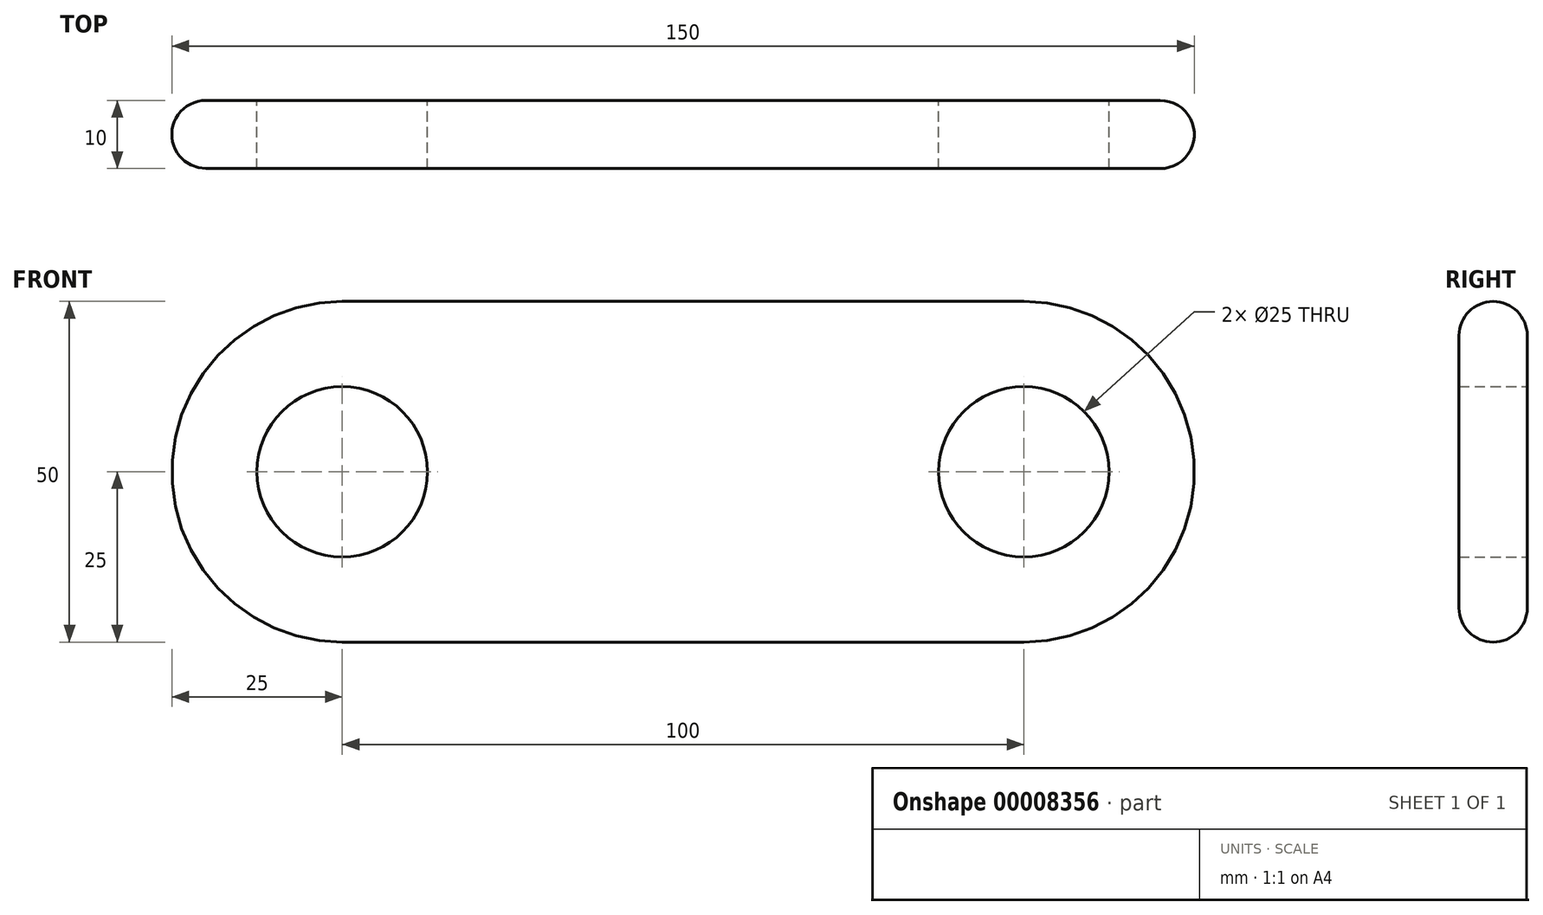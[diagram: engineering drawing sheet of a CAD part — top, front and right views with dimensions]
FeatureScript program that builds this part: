
annotation { "Feature Type Name" : "Feature", "Feature Type Description" : "" }
export const myFeature = defineFeature(function(context is Context, id is Id, definition is map)
    precondition{}
    {
        {
            var Q0;
            Q0=qCreatedBy(makeId("Front.planeOp"),FACE);
            var sketch = newSketch(context, id + "F0", { "sketchPlane" : qUnion([Q0])});
            skLineSegment(sketch, "E0.rect.bottom", {"start": v(50, 25) * mm, "end": v(-50, 25) * mm});
            skLineSegment(sketch, "E0.rect.top", {"start": v(50, -25) * mm, "end": v(-50, -25) * mm});
            skPoint(sketch, "E0.rect.middle", {"position": v(0, 0) * mm});
            skArc(sketch, "E1", {"start": v(-50, 25) * mm, "mid": v(-75, 0) * mm, "end": v(-50, -25) * mm});
            skArc(sketch, "E2", {"start": v(50, -25) * mm, "mid": v(75, 0) * mm, "end": v(50, 25) * mm});
            skCircle(sketch, "E3", {"center": v(-50, 0) * mm, "radius": 12.5 * mm});
            skCircle(sketch, "E4", {"center": v(50, 0) * mm, "radius": 12.5 * mm});
            skSolve(sketch);
        }
        {
            var Q0;
            Q0=makeQuery(id+"F0.imprint","IMPRINT",FACE,{"disambiguationData":[TD([[makeQuery(id+"F0.imprint","IMPRINT",EDGE,{"derivedFrom":sQuery(id+"F0.wireOp",EDGE,"E0.rect.bottom")}),1.0]])]});
            extrude(context, id + "F1", {"entities" : qUnion([Q0]), "depth" : 10 * mm});
        }
        {
            var Q0;
            Q0=makeQuery(id+"F1.opExtrude","CAP_EDGE",EDGE,{"disambiguationData":[OSD([sQuery(id+"F0.wireOp",EDGE,"E0.rect.top")])],"isStart":true});
            fillet(context, id + "F2", {"entities" : qUnion([Q0]), "radius" : 5 * mm, "tangentPropagation" : true, "allowEdgeOverflow" : false});
        }
        {
            var Q0;
            Q0=makeQuery(id+"F1.opExtrude","CAP_EDGE",EDGE,{"disambiguationData":[OSD([sQuery(id+"F0.wireOp",EDGE,"E0.rect.bottom")])],"isStart":false});
            fillet(context, id + "F3", {"entities" : qUnion([Q0]), "radius" : 5 * mm, "tangentPropagation" : true, "allowEdgeOverflow" : false});
        }
    });
